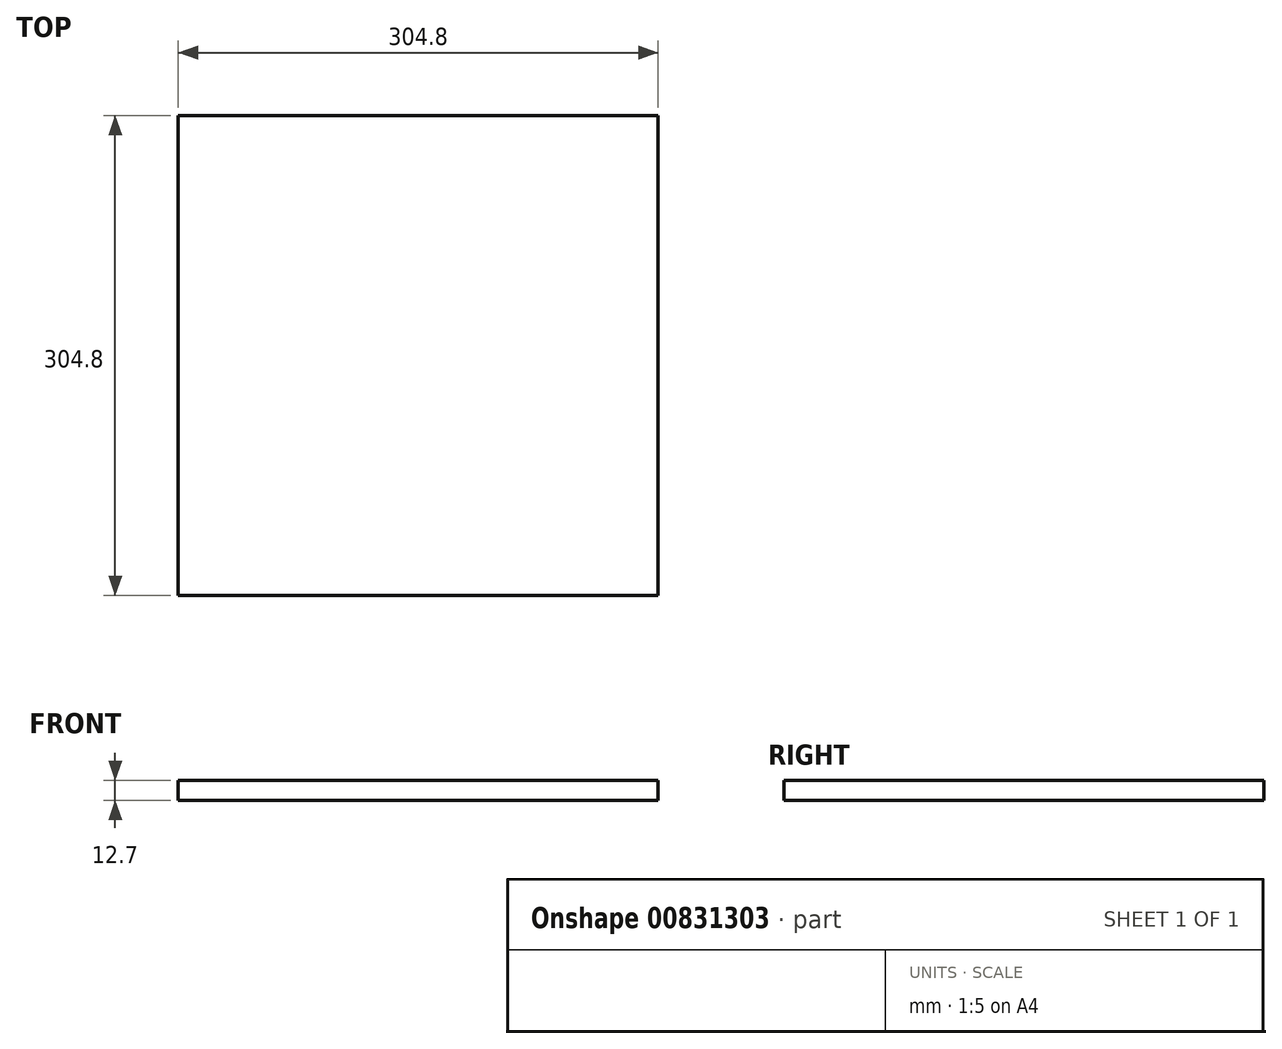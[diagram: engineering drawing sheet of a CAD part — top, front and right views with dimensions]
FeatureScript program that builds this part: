
annotation { "Feature Type Name" : "Feature", "Feature Type Description" : "" }
export const myFeature = defineFeature(function(context is Context, id is Id, definition is map)
    precondition{}
    {
        {
            var Q0;
            Q0=qCreatedBy(makeId("Top.planeOp"),FACE);
            var sketch = newSketch(context, id + "F0", { "sketchPlane" : qUnion([Q0])});
            skLineSegment(sketch, "E0.bottom", {"start": v(-152.4, 152.4) * mm, "end": v(152.4, 152.4) * mm});
            skLineSegment(sketch, "E0.top", {"start": v(-152.4, -152.4) * mm, "end": v(152.4, -152.4) * mm});
            skLineSegment(sketch, "E0.left", {"start": v(-152.4, 152.4) * mm, "end": v(-152.4, -152.4) * mm});
            skLineSegment(sketch, "E0.right", {"start": v(152.4, 152.4) * mm, "end": v(152.4, -152.4) * mm});
            skLineSegment(sketch, "E1", {"start": v(-152.4, 152.4) * mm, "end": v(152.4, -152.4) * mm, "construction": true});
            skSolve(sketch);
        }
        {
            var Q0;
            Q0 = qSketchRegion(id + "F0", true);
            extrude(context, id + "F1", {"entities" : qUnion([Q0]), "oppositeDirection" : true, "depth" : 12.7 * mm, "offsetDistance" : 25.4 * mm});
        }
    });
